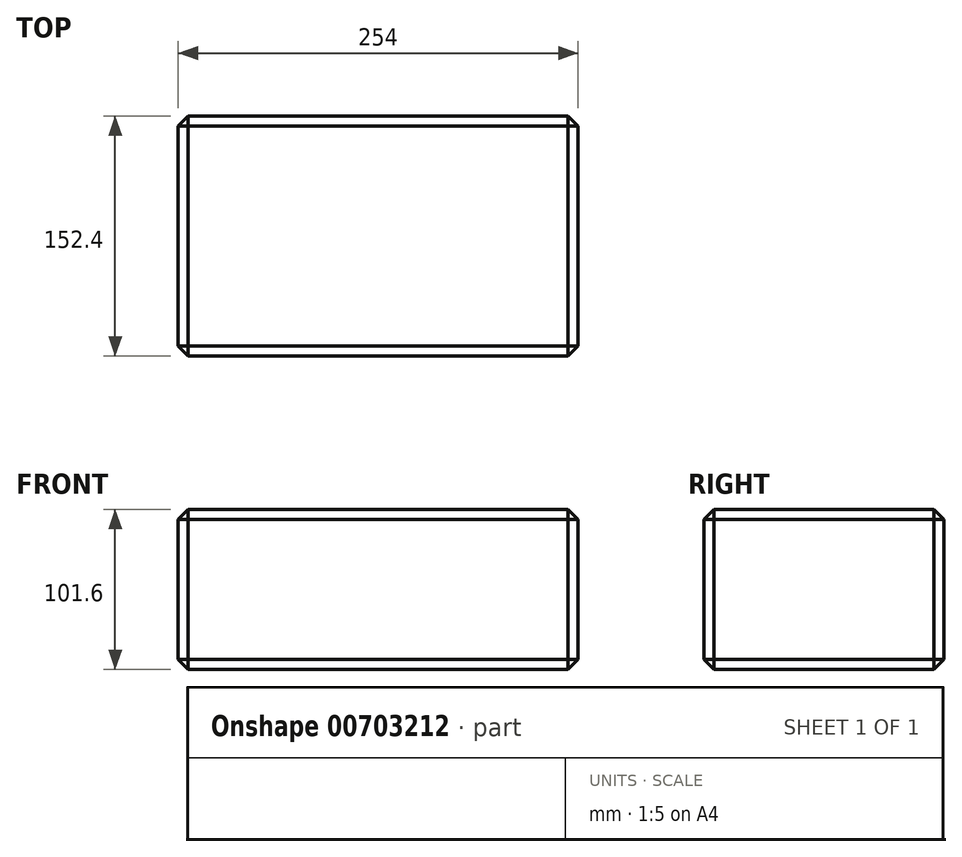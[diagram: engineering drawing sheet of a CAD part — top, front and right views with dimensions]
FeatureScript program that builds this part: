
annotation { "Feature Type Name" : "Feature", "Feature Type Description" : "" }
export const myFeature = defineFeature(function(context is Context, id is Id, definition is map)
    precondition{}
    {
        {
            var Q0;
            Q0=qCreatedBy(makeId("Top.planeOp"),FACE);
            var sketch = newSketch(context, id + "F0", { "sketchPlane" : qUnion([Q0])});
            skLineSegment(sketch, "E0", {"start": v(0, 0) * mm, "end": v(0, 76.2) * mm, "construction": true});
            skLineSegment(sketch, "E1", {"start": v(0, 0) * mm, "end": v(-127, 0) * mm, "construction": true});
            skLineSegment(sketch, "E2", {"start": v(-127, 0) * mm, "end": v(-127, 76.2) * mm, "construction": true});
            skLineSegment(sketch, "E3", {"start": v(-127, 76.2) * mm, "end": v(0, 76.2) * mm, "construction": true});
            skLineSegment(sketch, "E4.bottom", {"start": v(-127, 76.2) * mm, "end": v(127, 76.2) * mm});
            skLineSegment(sketch, "E4.top", {"start": v(-127, -76.2) * mm, "end": v(127, -76.2) * mm});
            skLineSegment(sketch, "E4.left", {"start": v(-127, 76.2) * mm, "end": v(-127, -76.2) * mm});
            skLineSegment(sketch, "E4.right", {"start": v(127, 76.2) * mm, "end": v(127, -76.2) * mm});
            skSolve(sketch);
        }
        {
            var Q0;
            Q0=makeQuery(id+"F0.imprint","IMPRINT",FACE,{"disambiguationData":[TD([[makeQuery(id+"F0.imprint","IMPRINT",EDGE,{"derivedFrom":sQuery(id+"F0.wireOp",EDGE,"E4.bottom")}),-1.0]])]});
            extrude(context, id + "F1", {"entities" : qUnion([Q0]), "depth" : 101.6 * mm, "offsetDistance" : 25.4 * mm});
        }
        {
            var Q0;
            Q0=makeQuery(id+"F1.opExtrude","CAP_EDGE",EDGE,{"disambiguationData":[OSD([sQuery(id+"F0.wireOp",EDGE,"E4.top")])],"isStart":false});
            var Q1;
            Q1=makeQuery(id+"F1.opExtrude","CAP_EDGE",EDGE,{"disambiguationData":[OSD([sQuery(id+"F0.wireOp",EDGE,"E4.right")])],"isStart":false});
            var Q2;
            Q2=makeQuery(id+"F1.opExtrude","CAP_FACE",FACE,{"disambiguationData":[OSD([sQuery(id+"F0.wireOp",EDGE,"E4.bottom"),sQuery(id+"F0.wireOp",EDGE,"E4.top"),sQuery(id+"F0.wireOp",EDGE,"E4.left"),sQuery(id+"F0.wireOp",EDGE,"E4.right")])],"isStart":false});
            var Q3;
            Q3=makeQuery(id+"F1.opExtrude","SWEPT_FACE",FACE,{"disambiguationData":[OSD([sQuery(id+"F0.wireOp",EDGE,"E4.right")])]});
            var Q4;
            Q4=makeQuery(id+"F1.opExtrude","SWEPT_FACE",FACE,{"disambiguationData":[OSD([sQuery(id+"F0.wireOp",EDGE,"E4.top")])]});
            var Q5;
            Q5=makeQuery(id+"F1.opExtrude","SWEPT_FACE",FACE,{"disambiguationData":[OSD([sQuery(id+"F0.wireOp",EDGE,"E4.bottom")])]});
            var Q6;
            Q6=makeQuery(id+"F1.opExtrude","CAP_FACE",FACE,{"disambiguationData":[OSD([sQuery(id+"F0.wireOp",EDGE,"E4.bottom"),sQuery(id+"F0.wireOp",EDGE,"E4.top"),sQuery(id+"F0.wireOp",EDGE,"E4.left"),sQuery(id+"F0.wireOp",EDGE,"E4.right")])],"isStart":true});
            var Q7;
            Q7=makeQuery(id+"F1.opExtrude","SWEPT_FACE",FACE,{"disambiguationData":[OSD([sQuery(id+"F0.wireOp",EDGE,"E4.left")])]});
            chamfer(context, id + "F2", {"entities" : qUnion([Q0, Q1, Q2, Q3, Q4, Q5, Q6, Q7]), "width" : 6.35 * mm, "tangentPropagation" : true});
        }
    });
